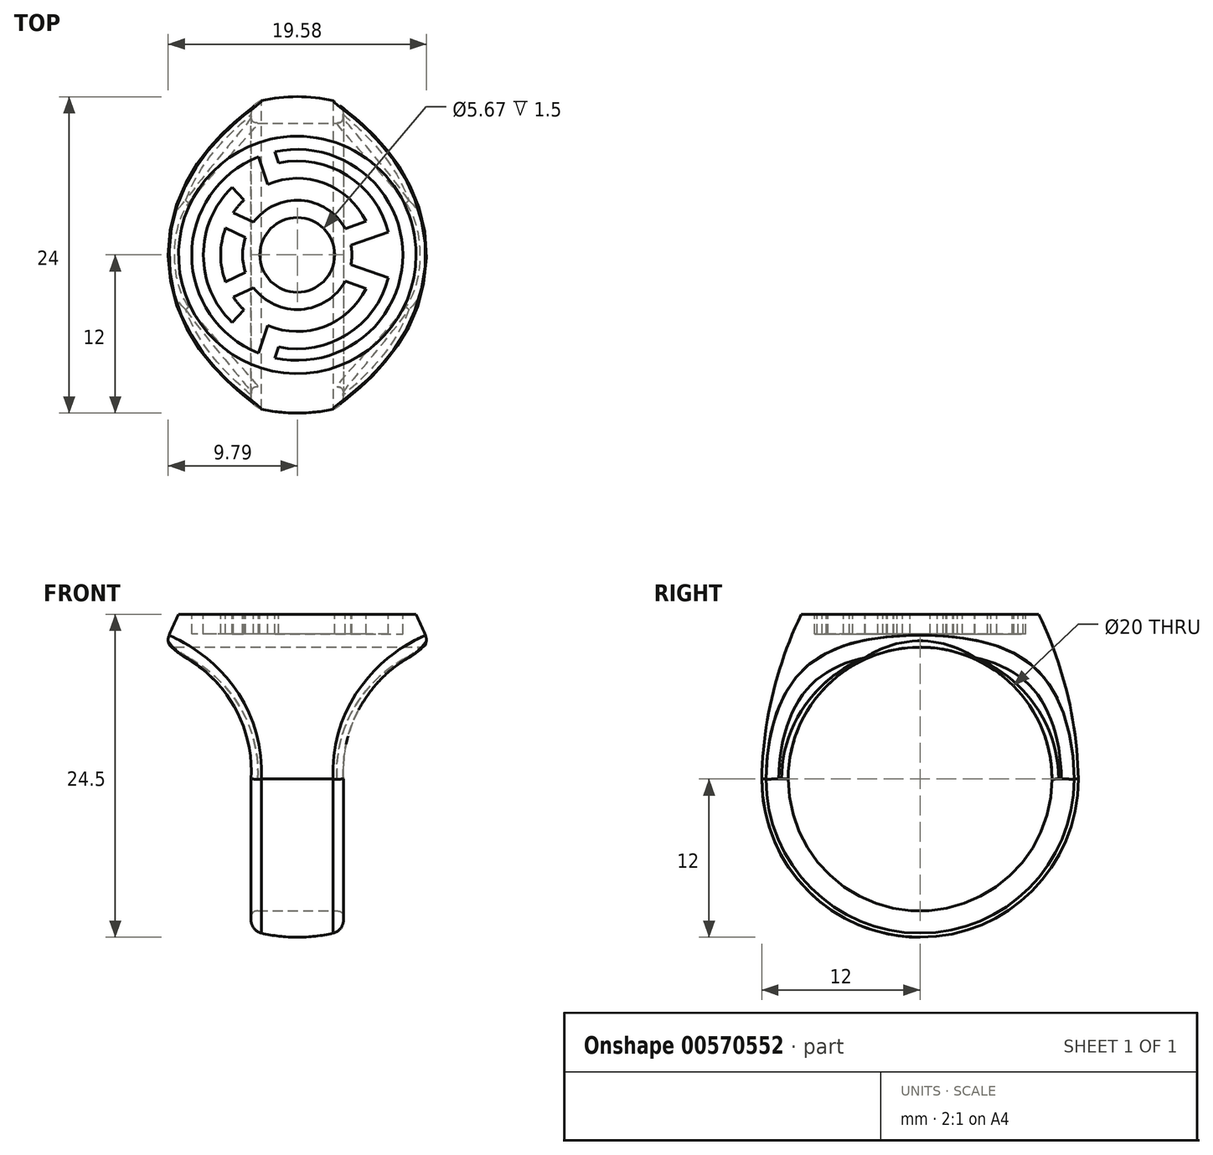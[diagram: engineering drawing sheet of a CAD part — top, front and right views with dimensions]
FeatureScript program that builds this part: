
annotation { "Feature Type Name" : "Feature", "Feature Type Description" : "" }
export const myFeature = defineFeature(function(context is Context, id is Id, definition is map)
    precondition{}
    {
        {
            var Q0;
            Q0=qCreatedBy(makeId("Right.planeOp"),FACE);
            var sketch = newSketch(context, id + "F0", { "sketchPlane" : qUnion([Q0])});
            skLineSegment(sketch, "E0", {"start": v(0, 0) * mm, "end": v(0, -24.5) * mm});
            skLineSegment(sketch, "E1", {"start": v(0, 0) * mm, "end": v(-9, 0) * mm});
            skArc(sketch, "E2", {"start": v(-12, -12.5) * mm, "mid": v(-8.49, -20.99) * mm, "end": v(0, -24.5) * mm});
            skLineSegment(sketch, "E3", {"start": v(0, -12.5) * mm, "end": v(-12, -12.5) * mm, "construction": true});
            skArc(sketch, "E4", {"start": v(-9, 0) * mm, "mid": v(-11.18, -6.09) * mm, "end": v(-12, -12.5) * mm});
            skSolve(sketch);
        }
        {
            var Q0;
            Q0=makeQuery(id+"F0.imprint","IMPRINT",FACE,{"disambiguationData":[TD([[makeQuery(id+"F0.imprint","IMPRINT",EDGE,{"derivedFrom":sQuery(id+"F0.wireOp",EDGE,"E0")}),-1.0]])]});
            var Q1;
            Q1=sQuery(id+"F0.wireOp",EDGE,"E0");
            revolve(context, id + "F1", {"entities" : qUnion([Q0]), "axis" : qUnion([Q1]), "revolveType" : RevolveType.FULL});
        }
        {
            var Q0;
            Q0=qCreatedBy(makeId("Right.planeOp"),FACE);
            var sketch = newSketch(context, id + "F2", { "sketchPlane" : qUnion([Q0])});
            skCircle(sketch, "E5", {"center": v(0, -12.5) * mm, "radius": 10 * mm});
            skSolve(sketch);
        }
        {
            var Q0;
            Q0=qSketchRegion(id+"F2",true);
            extrude(context, id + "F3", {"entities" : qUnion([Q0]), "operationType" : NewBodyOperationType.REMOVE, "oppositeDirection" : true, "depth" : 25 * mm, "offsetDistance" : 25 * mm, "symmetric" : true});
        }
        {
            var Q0;
            Q0=qCreatedBy(makeId("Front.planeOp"),FACE);
            var sketch = newSketch(context, id + "F4", { "sketchPlane" : qUnion([Q0])});
            skLineSegment(sketch, "E6", {"start": v(3.5, -26.5) * mm, "end": v(3.5, -12.5) * mm});
            skArc(sketch, "E7", {"start": v(10.15, -2.5) * mm, "mid": v(5.16, -6.39) * mm, "end": v(3.5, -12.5) * mm});
            skLineSegment(sketch, "E8", {"start": v(10.15, -2.5) * mm, "end": v(11.65, -2.5) * mm});
            skLineSegment(sketch, "E9", {"start": v(11.65, -2.5) * mm, "end": v(11.65, -26.5) * mm});
            skLineSegment(sketch, "E10", {"start": v(11.65, -26.5) * mm, "end": v(3.5, -26.5) * mm});
            skPoint(sketch, "E11.start.orphan", {"position": v(0, -24.5) * mm});
            skLineSegment(sketch, "E12", {"start": v(0, 0) * mm, "end": v(0, -24.5) * mm, "construction": true});
            skLineSegment(sketch, "E13.MirrorCS", {"start": v(-3.5, -26.5) * mm, "end": v(-3.5, -12.5) * mm});
            skArc(sketch, "E14.MirrorCS", {"start": v(-10.15, -2.5) * mm, "mid": v(-5.16, -6.39) * mm, "end": v(-3.5, -12.5) * mm});
            skLineSegment(sketch, "E15.MirrorCS", {"start": v(-11.65, -2.5) * mm, "end": v(-11.65, -26.5) * mm});
            skLineSegment(sketch, "E16.MirrorCS", {"start": v(-11.65, -26.5) * mm, "end": v(-3.5, -26.5) * mm});
            skLineSegment(sketch, "E17.MirrorCS", {"start": v(-10.15, -2.5) * mm, "end": v(-11.65, -2.5) * mm});
            skSolve(sketch);
        }
        {
            var Q0;
            Q0=qSketchRegion(id+"F4",true);
            extrude(context, id + "F5", {"entities" : qUnion([Q0]), "operationType" : NewBodyOperationType.REMOVE, "depth" : 25 * mm, "offsetDistance" : 25 * mm, "symmetric" : true});
        }
        {
            var Q0;
            Q0=makeQuery(id+"F1.opRevolve","SWEPT_FACE",FACE,{"disambiguationData":[OSD([sQuery(id+"F0.wireOp",EDGE,"E1")])]});
            var sketch = newSketch(context, id + "F6", { "sketchPlane" : qUnion([Q0])});
            skLineSegment(sketch, "E18", {"start": v(-8, 0) * mm, "end": v(8, 0) * mm, "construction": true});
            skArc(sketch, "E19", {"start": v(-2.95, 7.44) * mm, "mid": v(-8, 0) * mm, "end": v(-2.95, -7.44) * mm});
            skArc(sketch, "E20", {"start": v(-4.95, 5.12) * mm, "mid": v(-6.55, 2.78) * mm, "end": v(-7.12, 0) * mm});
            skArc(sketch, "E21", {"start": v(5.22, 2.54) * mm, "mid": v(2.05, 5.44) * mm, "end": v(-2.25, 5.36) * mm});
            skArc(sketch, "E22", {"start": v(3.63, 1.99) * mm, "mid": v(0.3, 4.13) * mm, "end": v(-3.32, 2.48) * mm});
            skArc(sketch, "E23", {"start": v(2.83, 0) * mm, "mid": v(0, 2.83) * mm, "end": v(-2.83, 0) * mm});
            skLineSegment(sketch, "E24", {"start": v(6.9, 1.74) * mm, "end": v(4.07, 0.75) * mm});
            skLineSegment(sketch, "E25", {"start": v(5.22, 2.54) * mm, "end": v(3.63, 1.99) * mm});
            skLineSegment(sketch, "E26", {"start": v(-3.32, 2.48) * mm, "end": v(-4.84, 3.2) * mm});
            skLineSegment(sketch, "E27", {"start": v(-3.93, 1.32) * mm, "end": v(-5.44, 2.04) * mm});
            skLineSegment(sketch, "E28", {"start": v(-1.7, 7.82) * mm, "end": v(-1.41, 6.98) * mm});
            skLineSegment(sketch, "E29", {"start": v(-2.25, 5.36) * mm, "end": v(-2.95, 7.44) * mm});
            skArc(sketch, "E30.trimOffspring", {"start": v(-3.93, 1.32) * mm, "mid": v(-4.09, 0.67) * mm, "end": v(-4.14, 0) * mm});
            skArc(sketch, "E31.trimOffspring", {"start": v(-5.44, 2.04) * mm, "mid": v(-5.71, 1.04) * mm, "end": v(-5.8, 0) * mm});
            skArc(sketch, "E32.trimOffspring", {"start": v(6.9, 1.74) * mm, "mid": v(3.8, 6.02) * mm, "end": v(-1.41, 6.98) * mm});
            skArc(sketch, "E33.trimOffspring", {"start": v(4.14, 0) * mm, "mid": v(4.13, 0.38) * mm, "end": v(4.07, 0.75) * mm});
            skLineSegment(sketch, "E34", {"start": v(-4.95, 5.12) * mm, "end": v(-4.04, 4.17) * mm});
            skArc(sketch, "E35.trimOffspring", {"start": v(-4.04, 4.17) * mm, "mid": v(-4.47, 3.71) * mm, "end": v(-4.84, 3.2) * mm});
            skArc(sketch, "E36.MirrorCS", {"start": v(2.83, 0) * mm, "mid": v(0, -2.83) * mm, "end": v(-2.83, 0) * mm});
            skArc(sketch, "E37.MirrorCS", {"start": v(4.14, 0) * mm, "mid": v(4.13, -0.38) * mm, "end": v(4.07, -0.75) * mm});
            skLineSegment(sketch, "E38.MirrorCS", {"start": v(6.9, -1.74) * mm, "end": v(4.07, -0.75) * mm});
            skArc(sketch, "E39.MirrorCS", {"start": v(6.9, -1.74) * mm, "mid": v(3.8, -6.02) * mm, "end": v(-1.41, -6.98) * mm});
            skLineSegment(sketch, "E40.MirrorCS", {"start": v(-1.7, -7.82) * mm, "end": v(-1.41, -6.98) * mm});
            skLineSegment(sketch, "E41.MirrorCS", {"start": v(-2.25, -5.36) * mm, "end": v(-2.95, -7.44) * mm});
            skArc(sketch, "E42.MirrorCS", {"start": v(5.22, -2.54) * mm, "mid": v(2.05, -5.44) * mm, "end": v(-2.25, -5.36) * mm});
            skLineSegment(sketch, "E43.MirrorCS", {"start": v(5.22, -2.54) * mm, "end": v(3.63, -1.99) * mm});
            skArc(sketch, "E44.MirrorCS", {"start": v(3.63, -1.99) * mm, "mid": v(0.3, -4.13) * mm, "end": v(-3.32, -2.48) * mm});
            skLineSegment(sketch, "E45.MirrorCS", {"start": v(-3.32, -2.48) * mm, "end": v(-4.84, -3.2) * mm});
            skArc(sketch, "E46.MirrorCS", {"start": v(-4.04, -4.17) * mm, "mid": v(-4.47, -3.71) * mm, "end": v(-4.84, -3.2) * mm});
            skLineSegment(sketch, "E47.MirrorCS", {"start": v(-4.95, -5.12) * mm, "end": v(-4.04, -4.17) * mm});
            skArc(sketch, "E48.MirrorCS", {"start": v(-4.95, -5.12) * mm, "mid": v(-6.55, -2.78) * mm, "end": v(-7.12, 0) * mm});
            skArc(sketch, "E49.MirrorCS", {"start": v(-3.93, -1.32) * mm, "mid": v(-4.09, -0.67) * mm, "end": v(-4.14, 0) * mm});
            skLineSegment(sketch, "E50.MirrorCS", {"start": v(-3.93, -1.32) * mm, "end": v(-5.44, -2.04) * mm});
            skArc(sketch, "E51.MirrorCS", {"start": v(-5.44, -2.04) * mm, "mid": v(-5.71, -1.04) * mm, "end": v(-5.8, 0) * mm});
            skArc(sketch, "E52.trimOffspring", {"start": v(-1.7, -7.82) * mm, "mid": v(8, 0) * mm, "end": v(-1.7, 7.82) * mm});
            skSolve(sketch);
        }
        {
            var Q0;
            Q0=qSketchRegion(id+"F6",true);
            var Q1;
            Q1=makeQuery(id+"F6.imprint","IMPRINT",FACE,{"disambiguationData":[TD([[makeQuery(id+"F6.imprint","IMPRINT",EDGE,{"derivedFrom":sQuery(id+"F6.wireOp",EDGE,"g20j87Mm-wGr7-AMiz-bI8b-qS7GuHKO57cL")}),1.0]])]});
            extrude(context, id + "F7", {"entities" : qUnion([Q0, Q1]), "operationType" : NewBodyOperationType.REMOVE, "oppositeDirection" : true, "depth" : 1.5 * mm, "offsetDistance" : 25 * mm});
        }
        {
            var Q0;
            Q0=makeQuery(id+"F5.boolean.opBoolean","INTERSECT",EDGE,{"disambiguationData":[OD(1.0)],"derivedFrom":[makeQuery(id+"F1.opRevolve","SWEPT_FACE",FACE,{"disambiguationData":[OSD([sQuery(id+"F0.wireOp",EDGE,"E4")])]}),makeQuery(id+"F5.opExtrude","SWEPT_FACE",FACE,{"disambiguationData":[OSD([sQuery(id+"F4.wireOp",EDGE,"E14.MirrorCS")])]})]});
            var Q1;
            Q1=makeQuery(id+"F5.boolean.opBoolean","INTERSECT",EDGE,{"derivedFrom":[makeQuery(id+"F1.opRevolve","SWEPT_FACE",FACE,{"disambiguationData":[OSD([sQuery(id+"F0.wireOp",EDGE,"E2")])]}),makeQuery(id+"F5.opExtrude","SWEPT_FACE",FACE,{"disambiguationData":[OSD([sQuery(id+"F4.wireOp",EDGE,"E13.MirrorCS")])]})]});
            var Q2;
            Q2=makeQuery(id+"F5.boolean.opBoolean","INTERSECT",EDGE,{"disambiguationData":[OD(1.0)],"derivedFrom":[makeQuery(id+"F1.opRevolve","SWEPT_FACE",FACE,{"disambiguationData":[OSD([sQuery(id+"F0.wireOp",EDGE,"E4")])]}),makeQuery(id+"F5.opExtrude","SWEPT_FACE",FACE,{"disambiguationData":[OSD([sQuery(id+"F4.wireOp",EDGE,"E7")])]})]});
            var Q3;
            Q3=makeQuery(id+"F5.boolean.opBoolean","INTERSECT",EDGE,{"derivedFrom":[makeQuery(id+"F1.opRevolve","SWEPT_FACE",FACE,{"disambiguationData":[OSD([sQuery(id+"F0.wireOp",EDGE,"E2")])]}),makeQuery(id+"F5.opExtrude","SWEPT_FACE",FACE,{"disambiguationData":[OSD([sQuery(id+"F4.wireOp",EDGE,"E6")])]})]});
            fillet(context, id + "F8", {"entities" : qUnion([Q0, Q1, Q2, Q3]), "radius" : 1 * mm, "allowEdgeOverflow" : false});
        }
        {
            var Q0;
            Q0=makeQuery(id+"F5.boolean.opBoolean","INTERSECT",EDGE,{"disambiguationData":[OD(1.0)],"derivedFrom":[makeQuery(id+"F3.boolean.opBoolean","COPY",FACE,{"derivedFrom":makeQuery(id+"F3.opExtrude","SWEPT_FACE",FACE,{"disambiguationData":[OSD([sQuery(id+"F2.wireOp",EDGE,"E5")])]})}),makeQuery(id+"F5.opExtrude","SWEPT_FACE",FACE,{"disambiguationData":[OSD([sQuery(id+"F4.wireOp",EDGE,"E14.MirrorCS")])]})]});
            var Q1;
            Q1=makeQuery(id+"F5.boolean.opBoolean","INTERSECT",EDGE,{"derivedFrom":[makeQuery(id+"F3.boolean.opBoolean","COPY",FACE,{"derivedFrom":makeQuery(id+"F3.opExtrude","SWEPT_FACE",FACE,{"disambiguationData":[OSD([sQuery(id+"F2.wireOp",EDGE,"E5")])]})}),makeQuery(id+"F5.opExtrude","SWEPT_FACE",FACE,{"disambiguationData":[OSD([sQuery(id+"F4.wireOp",EDGE,"E13.MirrorCS")])]})]});
            var Q2;
            Q2=makeQuery(id+"F5.boolean.opBoolean","INTERSECT",EDGE,{"disambiguationData":[OD(0.0)],"derivedFrom":[makeQuery(id+"F3.boolean.opBoolean","COPY",FACE,{"derivedFrom":makeQuery(id+"F3.opExtrude","SWEPT_FACE",FACE,{"disambiguationData":[OSD([sQuery(id+"F2.wireOp",EDGE,"E5")])]})}),makeQuery(id+"F5.opExtrude","SWEPT_FACE",FACE,{"disambiguationData":[OSD([sQuery(id+"F4.wireOp",EDGE,"E14.MirrorCS")])]})]});
            var Q3;
            Q3=makeQuery(id+"F5.boolean.opBoolean","INTERSECT",EDGE,{"disambiguationData":[OD(0.0)],"derivedFrom":[makeQuery(id+"F3.boolean.opBoolean","COPY",FACE,{"derivedFrom":makeQuery(id+"F3.opExtrude","SWEPT_FACE",FACE,{"disambiguationData":[OSD([sQuery(id+"F2.wireOp",EDGE,"E5")])]})}),makeQuery(id+"F5.opExtrude","SWEPT_FACE",FACE,{"disambiguationData":[OSD([sQuery(id+"F4.wireOp",EDGE,"E7")])]})]});
            var Q4;
            Q4=makeQuery(id+"F3.boolean.opBoolean","COPY",FACE,{"derivedFrom":makeQuery(id+"F3.opExtrude","SWEPT_FACE",FACE,{"disambiguationData":[OSD([sQuery(id+"F2.wireOp",EDGE,"E5")])]})});
            fillet(context, id + "F9", {"entities" : qUnion([Q0, Q1, Q2, Q3, Q4]), "radius" : .5 * mm, "rho" : 0.5, "crossSection" : FilletCrossSection.CONIC, "allowEdgeOverflow" : false});
        }
    });
